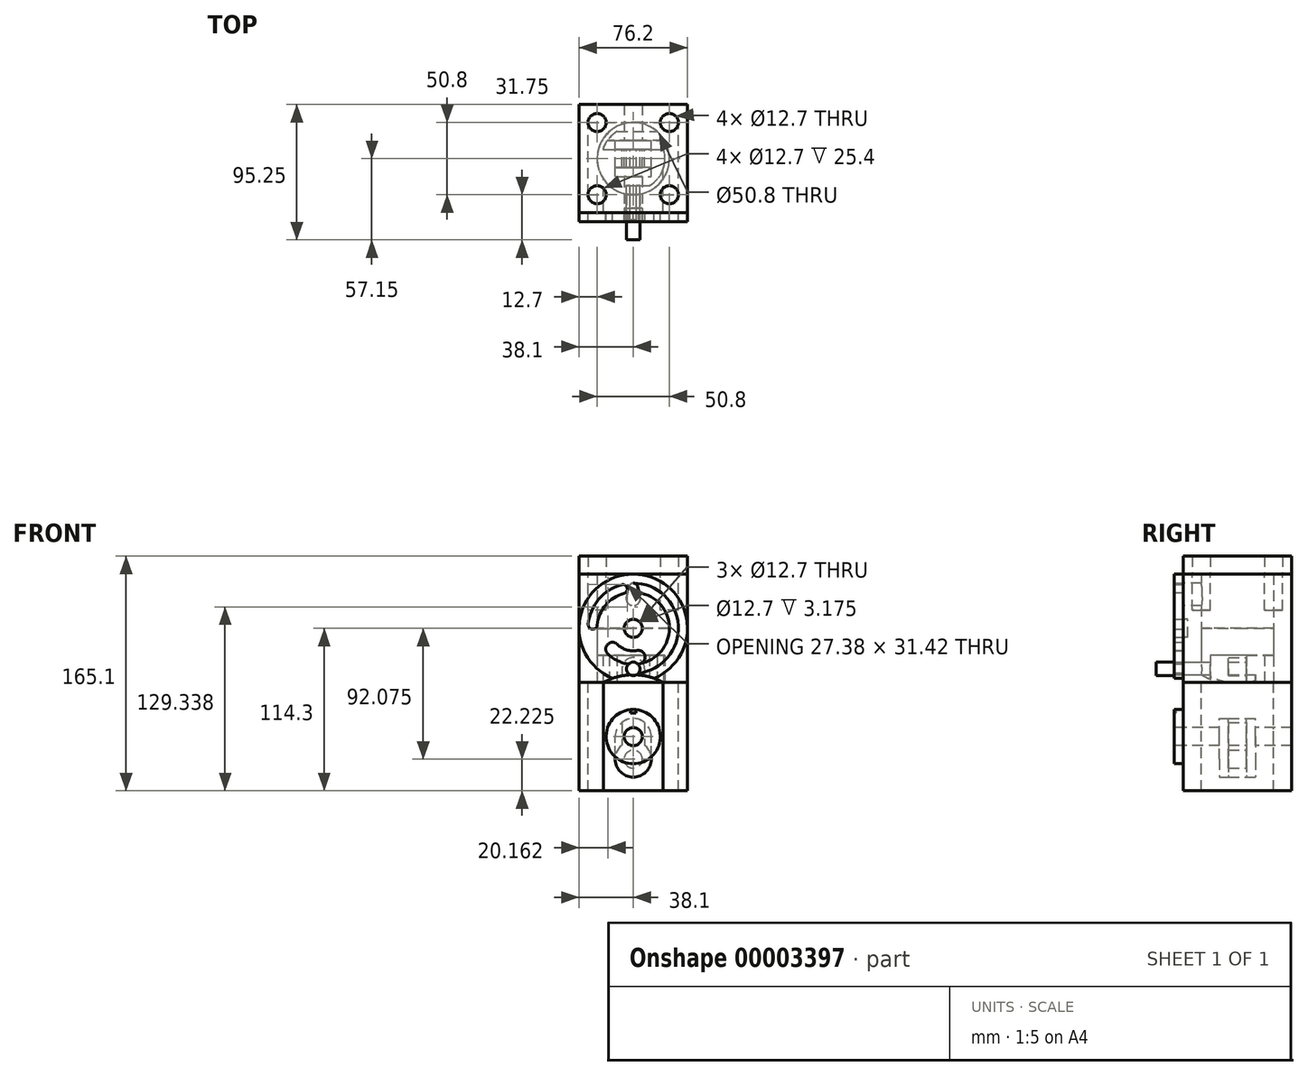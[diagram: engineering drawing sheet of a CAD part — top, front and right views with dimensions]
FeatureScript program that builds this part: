
annotation { "Feature Type Name" : "Feature", "Feature Type Description" : "" }
export const myFeature = defineFeature(function(context is Context, id is Id, definition is map)
    precondition{}
    {
        {
            var Q0;
            Q0=qCreatedBy(makeId("Top.planeOp"),FACE);
            var sketch = newSketch(context, id + "F0", { "sketchPlane" : qUnion([Q0])});
            skLineSegment(sketch, "E0.rect.bottom", {"start": v(38.1, 38.1) * mm, "end": v(-38.1, 38.1) * mm});
            skLineSegment(sketch, "E0.rect.top", {"start": v(38.1, -38.1) * mm, "end": v(-38.1, -38.1) * mm});
            skLineSegment(sketch, "E0.rect.left", {"start": v(38.1, 38.1) * mm, "end": v(38.1, -38.1) * mm});
            skLineSegment(sketch, "E0.rect.right", {"start": v(-38.1, 38.1) * mm, "end": v(-38.1, -38.1) * mm});
            skPoint(sketch, "E0.rect.middle", {"position": v(0, 0) * mm});
            skCircle(sketch, "E1", {"center": v(0, 0) * mm, "radius": 25.4 * mm});
            skSolve(sketch);
        }
        {
            var Q0;
            Q0=makeQuery(id+"F0.imprint","IMPRINT",FACE,{"disambiguationData":[TD([[makeQuery(id+"F0.imprint","IMPRINT",EDGE,{"derivedFrom":sQuery(id+"F0.wireOp",EDGE,"E0.rect.bottom")}),1.0]])]});
            extrude(context, id + "F1", {"entities" : qUnion([Q0]), "depth" : 76.2 * mm});
        }
        {
            var Q0;
            Q0=makeQuery(id+"F0.imprint","IMPRINT",FACE,{"disambiguationData":[TD([[makeQuery(id+"F0.imprint","IMPRINT",EDGE,{"derivedFrom":sQuery(id+"F0.wireOp",EDGE,"E1")}),1.0]])]});
            extrude(context, id + "F2", {"entities" : qUnion([Q0]), "depth" : 38.1 * mm});
        }
        {
            var Q0;
            Q0=makeQuery(id+"F1.opExtrude","CAP_FACE",FACE,{"disambiguationData":[OSD([sQuery(id+"F0.wireOp",EDGE,"E0.rect.bottom"),sQuery(id+"F0.wireOp",EDGE,"E0.rect.top"),sQuery(id+"F0.wireOp",EDGE,"E0.rect.left"),sQuery(id+"F0.wireOp",EDGE,"E0.rect.right"),sQuery(id+"F0.wireOp",EDGE,"E1")])],"isStart":false});
            var sketch = newSketch(context, id + "F3", { "sketchPlane" : qUnion([Q0])});
            skCircle(sketch, "E2", {"center": v(25.4, -25.4) * mm, "radius": 6.35 * mm});
            skCircle(sketch, "E3", {"center": v(25.4, 25.4) * mm, "radius": 6.35 * mm});
            skCircle(sketch, "E4", {"center": v(-25.4, 25.4) * mm, "radius": 6.35 * mm});
            skCircle(sketch, "E5", {"center": v(-25.4, -25.4) * mm, "radius": 6.35 * mm});
            skPoint(sketch, "E6.0", {"position": v(-38.1, 38.1) * mm});
            skPoint(sketch, "E7.0", {"position": v(38.1, -38.1) * mm});
            skSolve(sketch);
        }
        {
            var Q0;
            Q0=makeQuery(id+"F3.imprint","IMPRINT",FACE,{"disambiguationData":[TD([[makeQuery(id+"F3.imprint","IMPRINT",EDGE,{"derivedFrom":sQuery(id+"F3.wireOp",EDGE,"E4")}),1.0]])]});
            var Q1;
            Q1=makeQuery(id+"F3.imprint","IMPRINT",FACE,{"disambiguationData":[TD([[makeQuery(id+"F3.imprint","IMPRINT",EDGE,{"derivedFrom":sQuery(id+"F3.wireOp",EDGE,"E3")}),1.0]])]});
            var Q2;
            Q2=makeQuery(id+"F3.imprint","IMPRINT",FACE,{"disambiguationData":[TD([[makeQuery(id+"F3.imprint","IMPRINT",EDGE,{"derivedFrom":sQuery(id+"F3.wireOp",EDGE,"E2")}),1.0]])]});
            var Q3;
            Q3=makeQuery(id+"F3.imprint","IMPRINT",FACE,{"disambiguationData":[TD([[makeQuery(id+"F3.imprint","IMPRINT",EDGE,{"derivedFrom":sQuery(id+"F3.wireOp",EDGE,"E5")}),1.0]])]});
            extrude(context, id + "F4", {"entities" : qUnion([Q0, Q1, Q2, Q3]), "operationType" : NewBodyOperationType.REMOVE, "oppositeDirection" : true, "depth" : 25.4 * mm});
        }
        {
            var Q0;
            Q0=makeQuery(id+"F3.imprint","IMPRINT",FACE,{"disambiguationData":[TD([[makeQuery(id+"F3.imprint","IMPRINT",EDGE,{"derivedFrom":sQuery(id+"F3.wireOp",EDGE,"E2")}),-1.0]])]});
            var Q1;
            Q1=makeQuery(id+"F3.imprint","IMPRINT",FACE,{"disambiguationData":[TD([[makeQuery(id+"F3.imprint","IMPRINT",EDGE,{"derivedFrom":makeQuery(id+"F1.opExtrude","CAP_EDGE",EDGE,{"disambiguationData":[OSD([sQuery(id+"F0.wireOp",EDGE,"E1")])],"isStart":false})}),1.0]])]});
            extrude(context, id + "F5", {"entities" : qUnion([Q0, Q1]), "depth" : 12.7 * mm});
        }
        {
            var Q0;
            Q0=qCreatedBy(makeId("Right.planeOp"),FACE);
            var sketch = newSketch(context, id + "F6", { "sketchPlane" : qUnion([Q0])});
            skLineSegment(sketch, "E8", {"start": v(-107.9, -38.1) * mm, "end": v(101.54, -38.1) * mm});
            skLineSegment(sketch, "E9", {"start": v(-103.78, -53.98) * mm, "end": v(66.08, -53.97) * mm});
            skLineSegment(sketch, "E10.rect.bottom", {"start": v(38.1, -44.45) * mm, "end": v(-44.45, -44.45) * mm});
            skLineSegment(sketch, "E10.rect.top", {"start": v(38.1, -31.75) * mm, "end": v(-44.45, -31.75) * mm});
            skLineSegment(sketch, "E10.rect.left", {"start": v(38.1, -44.45) * mm, "end": v(38.1, -31.75) * mm});
            skLineSegment(sketch, "E10.rect.right", {"start": v(-44.45, -44.45) * mm, "end": v(-44.45, -31.75) * mm});
            skPoint(sketch, "E10.rect.middle", {"position": v(-3.17, -38.1) * mm});
            skLineSegment(sketch, "E11.rect.bottom", {"start": v(-6.35, -66.68) * mm, "end": v(-12.7, -66.68) * mm});
            skLineSegment(sketch, "E11.rect.top", {"start": v(-6.35, -9.52) * mm, "end": v(-12.7, -9.52) * mm});
            skLineSegment(sketch, "E11.rect.left", {"start": v(-6.35, -66.67) * mm, "end": v(-6.35, -9.52) * mm});
            skLineSegment(sketch, "E11.rect.right", {"start": v(-12.7, -66.68) * mm, "end": v(-12.7, -9.52) * mm});
            skPoint(sketch, "E11.rect.middle", {"position": v(-9.53, -38.1) * mm});
            skLineSegment(sketch, "E12.rect.bottom", {"start": v(6.35, -60.33) * mm, "end": v(-6.35, -60.33) * mm});
            skLineSegment(sketch, "E12.rect.top", {"start": v(6.35, -47.63) * mm, "end": v(-6.35, -47.63) * mm});
            skLineSegment(sketch, "E12.rect.left", {"start": v(6.35, -60.33) * mm, "end": v(6.35, -47.63) * mm});
            skLineSegment(sketch, "E12.rect.right", {"start": v(-6.35, -60.33) * mm, "end": v(-6.35, -47.63) * mm});
            skPoint(sketch, "E12.rect.middle", {"position": v(0, -53.98) * mm});
            skLineSegment(sketch, "E13.rect.bottom", {"start": v(12.7, -66.67) * mm, "end": v(6.35, -66.67) * mm});
            skLineSegment(sketch, "E13.rect.top", {"start": v(12.7, -9.52) * mm, "end": v(6.35, -9.52) * mm});
            skLineSegment(sketch, "E13.rect.left", {"start": v(12.7, -66.67) * mm, "end": v(12.7, -9.52) * mm});
            skLineSegment(sketch, "E13.rect.right", {"start": v(6.35, -66.67) * mm, "end": v(6.35, -9.52) * mm});
            skPoint(sketch, "E13.rect.middle", {"position": v(9.52, -38.1) * mm});
            skLineSegment(sketch, "E14.0", {"start": v(38.1, 0) * mm, "end": v(-38.1, 0) * mm, "construction": true});
            skSolve(sketch);
        }
        {
            var Q0;
            {var subQ1=sQuery(id+"F6.wireOp",EDGE,"E8");var subQ5=sQuery(id+"F6.wireOp",EDGE,"E10.rect.right");var subQ6=makeQuery(id+"F6.imprint","INTERSECT",VERTEX,{"derivedFrom":[subQ1,subQ5]});Q0=makeQuery(id+"F6.imprint","IMPRINT",FACE,{"disambiguationData":[TD([[makeQuery(id+"F6.imprint","IMPRINT",EDGE,{"disambiguationData":[TD([[subQ6,-1.0]])],"derivedFrom":subQ1}),1.0]])]});}
            var Q1;
            {var subQ0=sQuery(id+"F6.wireOp",EDGE,"E11.rect.right");var subQ1=sQuery(id+"F6.wireOp",EDGE,"E8");var subQ2=makeQuery(id+"F6.imprint","INTERSECT",VERTEX,{"derivedFrom":[subQ1,subQ0]});Q1=makeQuery(id+"F6.imprint","IMPRINT",FACE,{"disambiguationData":[TD([[makeQuery(id+"F6.imprint","IMPRINT",EDGE,{"disambiguationData":[TD([[subQ2,-1.0]])],"derivedFrom":subQ1}),1.0]])]});}
            var Q2;
            {var subQ3=sQuery(id+"F6.wireOp",EDGE,"E11.rect.bottom");Q2=makeQuery(id+"F6.imprint","IMPRINT",FACE,{"disambiguationData":[TD([[makeQuery(id+"F6.imprint","IMPRINT",EDGE,{"derivedFrom":subQ3}),-1.0]])]});}
            var Q3;
            {var subQ3=sQuery(id+"F6.wireOp",EDGE,"E11.rect.top");Q3=makeQuery(id+"F6.imprint","IMPRINT",FACE,{"disambiguationData":[TD([[makeQuery(id+"F6.imprint","IMPRINT",EDGE,{"derivedFrom":subQ3}),1.0]])]});}
            var Q4;
            {var subQ0=sQuery(id+"F6.wireOp",EDGE,"E13.rect.right");var subQ1=sQuery(id+"F6.wireOp",EDGE,"E8");var subQ2=makeQuery(id+"F6.imprint","INTERSECT",VERTEX,{"derivedFrom":[subQ1,subQ0]});Q4=makeQuery(id+"F6.imprint","IMPRINT",FACE,{"disambiguationData":[TD([[makeQuery(id+"F6.imprint","IMPRINT",EDGE,{"disambiguationData":[TD([[subQ2,-1.0]])],"derivedFrom":subQ1}),1.0]])]});}
            var Q5;
            {var subQ4=sQuery(id+"F6.wireOp",EDGE,"E13.rect.bottom");Q5=makeQuery(id+"F6.imprint","IMPRINT",FACE,{"disambiguationData":[TD([[makeQuery(id+"F6.imprint","IMPRINT",EDGE,{"derivedFrom":subQ4}),-1.0]])]});}
            var Q6;
            {var subQ3=sQuery(id+"F6.wireOp",EDGE,"E13.rect.top");Q6=makeQuery(id+"F6.imprint","IMPRINT",FACE,{"disambiguationData":[TD([[makeQuery(id+"F6.imprint","IMPRINT",EDGE,{"derivedFrom":subQ3}),1.0]])]});}
            var Q7;
            {var subQ1=sQuery(id+"F6.wireOp",EDGE,"E8");var subQ5=sQuery(id+"F6.wireOp",EDGE,"E10.rect.left");var subQ6=makeQuery(id+"F6.imprint","INTERSECT",VERTEX,{"derivedFrom":[subQ1,subQ5]});Q7=makeQuery(id+"F6.imprint","IMPRINT",FACE,{"disambiguationData":[TD([[makeQuery(id+"F6.imprint","IMPRINT",EDGE,{"disambiguationData":[TD([[subQ6,1.0]])],"derivedFrom":subQ1}),1.0]])]});}
            var Q8;
            Q8=sQuery(id+"F6.wireOp",EDGE,"E8");
            revolve(context, id + "F7", {"entities" : qUnion([Q0, Q1, Q2, Q3, Q4, Q5, Q6, Q7]), "axis" : qUnion([Q8]), "revolveType" : RevolveType.FULL});
        }
        {
            var Q0;
            {var subQ3=sQuery(id+"F6.wireOp",EDGE,"E12.rect.top");Q0=makeQuery(id+"F6.imprint","IMPRINT",FACE,{"disambiguationData":[TD([[makeQuery(id+"F6.imprint","IMPRINT",EDGE,{"derivedFrom":subQ3}),1.0]])]});}
            var Q1;
            Q1=sQuery(id+"F6.wireOp",EDGE,"E9");
            revolve(context, id + "F8", {"operationType" : NewBodyOperationType.ADD, "entities" : qUnion([Q0]), "axis" : qUnion([Q1]), "revolveType" : RevolveType.FULL});
        }
        {
            var Q0;
            Q0=makeQuery(id+"F2.opExtrude","CAP_FACE",FACE,{"disambiguationData":[OSD([sQuery(id+"F0.wireOp",EDGE,"E1")])],"isStart":true});
            var sketch = newSketch(context, id + "F9", { "sketchPlane" : qUnion([Q0])});
            skLineSegment(sketch, "E15.rect.bottom", {"start": v(-21.3, -6.35) * mm, "end": v(21.3, -6.35) * mm});
            skLineSegment(sketch, "E15.rect.top", {"start": v(-21.3, 6.35) * mm, "end": v(21.3, 6.35) * mm});
            skLineSegment(sketch, "E15.rect.left", {"start": v(-21.3, -6.35) * mm, "end": v(-21.3, 6.35) * mm, "construction": true});
            skLineSegment(sketch, "E15.rect.right", {"start": v(21.3, -6.35) * mm, "end": v(21.3, 6.35) * mm, "construction": true});
            skPoint(sketch, "E15.rect.middle", {"position": v(0, 0) * mm});
            skCircle(sketch, "E16", {"center": v(0, 0) * mm, "radius": 22.23 * mm});
            skLineSegment(sketch, "E17", {"start": v(-16.8, 19.05) * mm, "end": v(16.8, 19.05) * mm});
            skCircle(sketch, "E18.0", {"center": v(0, 0) * mm, "radius": 25.4 * mm});
            skLineSegment(sketch, "E19", {"start": v(0, 0) * mm, "end": v(-10.7, 0) * mm, "construction": true});
            skLineSegment(sketch, "E20.0.MirrorCS", {"start": v(-16.8, -19.05) * mm, "end": v(16.8, -19.05) * mm});
            skSolve(sketch);
        }
        {
            var Q0;
            {var subQ2=sQuery(id+"F9.wireOp",EDGE,"E15.rect.bottom");Q0=makeQuery(id+"F9.imprint","IMPRINT",FACE,{"disambiguationData":[TD([[makeQuery(id+"F9.imprint","IMPRINT",EDGE,{"derivedFrom":subQ2}),1.0]])]});}
            var Q1;
            {var subQ0=sQuery(id+"F9.wireOp",EDGE,"E17");var subQ1=sQuery(id+"F9.wireOp",EDGE,"E16");var subQ3=makeQuery(id+"F9.imprint","INTERSECT",VERTEX,{"disambiguationData":[OD(0.0)],"derivedFrom":[subQ1,subQ0]});Q1=makeQuery(id+"F9.imprint","IMPRINT",FACE,{"disambiguationData":[TD([[makeQuery(id+"F9.imprint","IMPRINT",EDGE,{"disambiguationData":[TD([[subQ3,-1.0]])],"derivedFrom":subQ1}),1.0]])]});}
            var Q2;
            {var subQ1=sQuery(id+"F9.wireOp",EDGE,"E17");var subQ4=sQuery(id+"F9.wireOp",EDGE,"E16");var subQ5=makeQuery(id+"F9.imprint","INTERSECT",VERTEX,{"disambiguationData":[OD(0.0)],"derivedFrom":[subQ4,subQ1]});Q2=makeQuery(id+"F9.imprint","IMPRINT",FACE,{"disambiguationData":[TD([[makeQuery(id+"F9.imprint","IMPRINT",EDGE,{"disambiguationData":[TD([[subQ5,-1.0]])],"derivedFrom":subQ4}),-1.0]])]});}
            var Q3;
            {var subQ0=sQuery(id+"F9.wireOp",EDGE,"E17");var subQ1=sQuery(id+"F9.wireOp",EDGE,"E16");var subQ3=makeQuery(id+"F9.imprint","INTERSECT",VERTEX,{"disambiguationData":[OD(0.0)],"derivedFrom":[subQ1,subQ0]});var subQ4=sQuery(id+"F9.wireOp",EDGE,"E20.0.MirrorCS");var subQ6=makeQuery(id+"F9.imprint","INTERSECT",VERTEX,{"disambiguationData":[OD(0.0)],"derivedFrom":[subQ1,subQ4]});Q3=qUnion([makeQuery(id+"F9.imprint","IMPRINT",FACE,{"disambiguationData":[TD([[makeQuery(id+"F9.imprint","IMPRINT",EDGE,{"disambiguationData":[TD([[subQ3,-1.0]])],"derivedFrom":subQ1}),1.0]])]}),makeQuery(id+"F9.imprint","IMPRINT",FACE,{"disambiguationData":[TD([[makeQuery(id+"F9.imprint","IMPRINT",EDGE,{"disambiguationData":[TD([[subQ6,-1.0]])],"derivedFrom":subQ1}),1.0]])]})]);}
            var Q4;
            {var subQ0=sQuery(id+"F9.wireOp",EDGE,"E20.0.MirrorCS");var subQ1=sQuery(id+"F9.wireOp",EDGE,"E16");var subQ5=makeQuery(id+"F9.imprint","INTERSECT",VERTEX,{"disambiguationData":[OD(0.0)],"derivedFrom":[subQ1,subQ0]});Q4=makeQuery(id+"F9.imprint","IMPRINT",FACE,{"disambiguationData":[TD([[makeQuery(id+"F9.imprint","IMPRINT",EDGE,{"disambiguationData":[TD([[subQ5,-1.0]])],"derivedFrom":subQ1}),-1.0]])]});}
            extrude(context, id + "F10", {"entities" : qUnion([Q0, Q1, Q2, Q3, Q4]), "operationType" : NewBodyOperationType.REMOVE, "oppositeDirection" : true, "depth" : 19.05 * mm});
        }
        {
            var Q0;
            Q0=makeQuery(id+"F10.boolean.opBoolean","COPY",FACE,{"derivedFrom":makeQuery(id+"F10.opExtrude","SWEPT_FACE",FACE,{"disambiguationData":[OSD([sQuery(id+"F9.wireOp",EDGE,"E17")])]})});
            var sketch = newSketch(context, id + "F11", { "sketchPlane" : qUnion([Q0])});
            skCircle(sketch, "E21", {"center": v(0, 9.53) * mm, "radius": 4.76 * mm});
            skLineSegment(sketch, "E22", {"start": v(-16.8, 0) * mm, "end": v(16.8, 19.05) * mm, "construction": true});
            skSolve(sketch);
        }
        {
            var Q0;
            Q0=makeQuery(id+"F11.imprint","IMPRINT",FACE,{"disambiguationData":[TD([[makeQuery(id+"F11.imprint","IMPRINT",EDGE,{"derivedFrom":sQuery(id+"F11.wireOp",EDGE,"E21")}),1.0]])]});
            extrude(context, id + "F12", {"entities" : qUnion([Q0]), "operationType" : NewBodyOperationType.REMOVE, "endBound" : BoundingType.THROUGH_ALL, "oppositeDirection" : true, "depth" : 25.4 * mm});
        }
        {
            var Q0;
            Q0=qCreatedBy(makeId("Front.planeOp"),FACE);
            var sketch = newSketch(context, id + "F13", { "sketchPlane" : qUnion([Q0])});
            skCircle(sketch, "E23.0", {"center": v(0, -53.98) * mm, "radius": 6.35 * mm});
            skCircle(sketch, "E23.1", {"center": v(0, 9.53) * mm, "radius": 4.76 * mm});
            skLineSegment(sketch, "E24.0", {"start": v(-21.3, 19.05) * mm, "end": v(21.3, 19.05) * mm});
            skCircle(sketch, "E25", {"center": v(0, 9.53) * mm, "radius": 7.94 * mm});
            skCircle(sketch, "E26", {"center": v(0, -53.98) * mm, "radius": 12.7 * mm});
            skLineSegment(sketch, "E27", {"start": v(7.94, 9.53) * mm, "end": v(7.94, -44.06) * mm});
            skLineSegment(sketch, "E28", {"start": v(-7.94, 9.52) * mm, "end": v(-7.94, -44.06) * mm});
            skSolve(sketch);
        }
        {
            var Q0;
            Q0=makeQuery(id+"F13.imprint","IMPRINT",FACE,{"disambiguationData":[TD([[makeQuery(id+"F13.imprint","IMPRINT",EDGE,{"derivedFrom":sQuery(id+"F13.wireOp",EDGE,"E23.1")}),-1.0]])]});
            var Q1;
            {var subQ1=sQuery(id+"F13.wireOp",EDGE,"E27");Q1=makeQuery(id+"F13.imprint","IMPRINT",FACE,{"disambiguationData":[TD([[makeQuery(id+"F13.imprint","IMPRINT",EDGE,{"derivedFrom":subQ1}),-1.0]])]});}
            var Q2;
            Q2=makeQuery(id+"F13.imprint","IMPRINT",FACE,{"disambiguationData":[TD([[makeQuery(id+"F13.imprint","IMPRINT",EDGE,{"derivedFrom":sQuery(id+"F13.wireOp",EDGE,"E23.0")}),-1.0]])]});
            extrude(context, id + "F14", {"entities" : qUnion([Q0, Q1, Q2]), "endBound" : BoundingType.SYMMETRIC, "depth" : 12.7 * mm});
        }
        {
            var Q0;
            Q0=makeQuery(id+"F11.imprint","IMPRINT",FACE,{"disambiguationData":[TD([[makeQuery(id+"F11.imprint","IMPRINT",EDGE,{"derivedFrom":sQuery(id+"F11.wireOp",EDGE,"E21")}),1.0]])]});
            extrude(context, id + "F15", {"entities" : qUnion([Q0]), "oppositeDirection" : true, "depth" : 38.1 * mm});
        }
        {
            var Q0;
            {var subQ0=sQuery(id+"F6.wireOp",EDGE,"E13.rect.left");Q0=makeQuery(id+"F7.opRevolve","SWEPT_FACE",FACE,{"disambiguationData":[OSD([subQ0]),TDD([makeQuery(id+"F6.imprint","IMPRINT",EDGE,{"disambiguationData":[TD([[makeQuery(id+"F6.imprint","INTERSECT",VERTEX,{"derivedFrom":[sQuery(id+"F6.wireOp",EDGE,"E13.rect.top"),subQ0]}),1.0]])],"derivedFrom":subQ0})])]});}
            var sketch = newSketch(context, id + "F16", { "sketchPlane" : qUnion([Q0])});
            skArc(sketch, "E29.0.0", {"start": v(-7.94, 9.53) * mm, "mid": v(0, 17.46) * mm, "end": v(7.94, 9.52) * mm});
            skArc(sketch, "E29.0.2", {"start": v(7.94, -44.06) * mm, "mid": v(0, -66.67) * mm, "end": v(-7.94, -44.06) * mm});
            skCircle(sketch, "E30.0", {"center": v(0, -38.1) * mm, "radius": 6.35 * mm});
            skArc(sketch, "E31", {"start": v(12.7, -38.1) * mm, "mid": v(0, -25.4) * mm, "end": v(-12.7, -38.1) * mm});
            skLineSegment(sketch, "E32", {"start": v(12.7, -38.1) * mm, "end": v(12.7, -53.98) * mm});
            skLineSegment(sketch, "E33", {"start": v(-12.7, -38.1) * mm, "end": v(-12.7, -53.98) * mm});
            skCircle(sketch, "E34", {"center": v(0, -38.1) * mm, "radius": 43.5 * mm});
            skSolve(sketch);
        }
        {
            var Q0;
            Q0=makeQuery(id+"F16.imprint","IMPRINT",FACE,{"disambiguationData":[TD([[makeQuery(id+"F16.imprint","IMPRINT",EDGE,{"derivedFrom":sQuery(id+"F16.wireOp",EDGE,"E34")}),1.0]])]});
            var Q1;
            Q1=makeQuery(id+"F16.imprint","IMPRINT",FACE,{"disambiguationData":[TD([[makeQuery(id+"F16.imprint","IMPRINT",EDGE,{"derivedFrom":sQuery(id+"F16.wireOp",EDGE,"E31")}),-1.0]])]});
            extrude(context, id + "F17", {"entities" : qUnion([Q0, Q1]), "operationType" : NewBodyOperationType.REMOVE, "oppositeDirection" : true, "depth" : 57.32 * mm});
        }
        {
            var Q0;
            Q0=makeQuery(id+"F1.opExtrude","CAP_FACE",FACE,{"disambiguationData":[OSD([sQuery(id+"F0.wireOp",EDGE,"E0.rect.bottom"),sQuery(id+"F0.wireOp",EDGE,"E0.rect.top"),sQuery(id+"F0.wireOp",EDGE,"E0.rect.left"),sQuery(id+"F0.wireOp",EDGE,"E0.rect.right"),sQuery(id+"F0.wireOp",EDGE,"E1")])],"isStart":true});
            var sketch = newSketch(context, id + "F18", { "sketchPlane" : qUnion([Q0])});
            skLineSegment(sketch, "E35.0", {"start": v(-38.1, -38.1) * mm, "end": v(-38.1, 38.1) * mm});
            skLineSegment(sketch, "E35.1", {"start": v(38.1, 38.1) * mm, "end": v(-38.1, 38.1) * mm});
            skLineSegment(sketch, "E35.2", {"start": v(38.1, -38.1) * mm, "end": v(-38.1, -38.1) * mm});
            skLineSegment(sketch, "E35.3", {"start": v(38.1, -38.1) * mm, "end": v(38.1, 38.1) * mm});
            skLineSegment(sketch, "E36.rect.bottom", {"start": v(-31.75, 25.4) * mm, "end": v(31.75, 25.4) * mm});
            skLineSegment(sketch, "E36.rect.top", {"start": v(-31.75, -25.4) * mm, "end": v(31.75, -25.4) * mm});
            skLineSegment(sketch, "E36.rect.left", {"start": v(-31.75, 25.4) * mm, "end": v(-31.75, -25.4) * mm});
            skLineSegment(sketch, "E36.rect.right", {"start": v(31.75, 25.4) * mm, "end": v(31.75, -25.4) * mm});
            skPoint(sketch, "E36.rect.middle", {"position": v(0, 0) * mm});
            skSolve(sketch);
        }
        {
            var Q0;
            Q0=makeQuery(id+"F18.imprint","IMPRINT",FACE,{"disambiguationData":[TD([[makeQuery(id+"F18.imprint","IMPRINT",EDGE,{"derivedFrom":sQuery(id+"F18.wireOp",EDGE,"E35.0")}),-1.0]])]});
            extrude(context, id + "F19", {"entities" : qUnion([Q0]), "depth" : 76.2 * mm});
        }
        {
            var Q0;
            Q0=makeQuery(id+"F7.opRevolve","SWEPT_BODY",BODY,{"disambiguationData":[OSD([sQuery(id+"F6.wireOp",EDGE,"E8"),sQuery(id+"F6.wireOp",EDGE,"E10.rect.top"),sQuery(id+"F6.wireOp",EDGE,"E10.rect.right"),sQuery(id+"F6.wireOp",EDGE,"E11.rect.top"),sQuery(id+"F6.wireOp",EDGE,"E11.rect.left"),sQuery(id+"F6.wireOp",EDGE,"E11.rect.right")])]});
            var Q1;
            Q1=makeQuery(id+"F19.opExtrude","SWEPT_BODY",BODY,{"disambiguationData":[OSD([sQuery(id+"F18.wireOp",EDGE,"E35.0"),sQuery(id+"F18.wireOp",EDGE,"E35.1"),sQuery(id+"F18.wireOp",EDGE,"E35.2"),sQuery(id+"F18.wireOp",EDGE,"E35.3"),sQuery(id+"F18.wireOp",EDGE,"E36.rect.bottom"),sQuery(id+"F18.wireOp",EDGE,"E36.rect.top"),sQuery(id+"F18.wireOp",EDGE,"E36.rect.left"),sQuery(id+"F18.wireOp",EDGE,"E36.rect.right")])]});
            booleanBodies(context, id + "F20", {"operationType" : BooleanOperationType.SUBTRACTION, "tools" : qUnion([Q0]), "targets" : qUnion([Q1]), "keepTools" : true});
        }
        {
            var Q0;
            Q0=makeQuery(id+"F1.opExtrude","SWEPT_FACE",FACE,{"disambiguationData":[OSD([sQuery(id+"F0.wireOp",EDGE,"E0.rect.top")])]});
            var sketch = newSketch(context, id + "F21", { "sketchPlane" : qUnion([Q0])});
            skLineSegment(sketch, "E37", {"start": v(-38.1, 0) * mm, "end": v(38.1, 76.2) * mm, "construction": true});
            skCircle(sketch, "E38", {"center": v(0, 38.1) * mm, "radius": 31.75 * mm});
            skCircle(sketch, "E39", {"center": v(0, 38.1) * mm, "radius": 25.4 * mm});
            skCircle(sketch, "E40", {"center": v(0, 38.1) * mm, "radius": 15.88 * mm});
            skArc(sketch, "E41", {"start": v(-6.57, 62.63) * mm, "mid": v(-4.33, 66.52) * mm, "end": v(-8.22, 68.77) * mm});
            skLineSegment(sketch, "E42", {"start": v(0, 38.1) * mm, "end": v(-38.1, 38.1) * mm, "construction": true});
            skLineSegment(sketch, "E43", {"start": v(0, 38.1) * mm, "end": v(-7.4, 65.7) * mm, "construction": true});
            skArc(sketch, "E44", {"start": v(-31.63, 40.87) * mm, "mid": v(-28.74, 37.43) * mm, "end": v(-25.3, 40.31) * mm});
            skLineSegment(sketch, "E45", {"start": v(0, 38.1) * mm, "end": v(-28.47, 40.6) * mm, "construction": true});
            skArc(sketch, "E46", {"start": v(-11.23, 26.87) * mm, "mid": v(-17.96, 26.87) * mm, "end": v(-17.96, 20.14) * mm});
            skArc(sketch, "E47", {"start": v(4.41, 13.09) * mm, "mid": v(8.27, 18.6) * mm, "end": v(2.76, 22.47) * mm});
            skLineSegment(sketch, "E48", {"start": v(0, 38.1) * mm, "end": v(-14.6, 23.5) * mm, "construction": true});
            skLineSegment(sketch, "E49", {"start": v(0, 38.1) * mm, "end": v(3.58, 17.78) * mm, "construction": true});
            skCircle(sketch, "E50", {"center": v(0, 38.1) * mm, "radius": 38.1 * mm});
            skCircle(sketch, "E51", {"center": v(0, 38.1) * mm, "radius": 6.35 * mm});
            skArc(sketch, "E52", {"start": v(3.11, 67.3) * mm, "mid": v(0, 69.85) * mm, "end": v(-3.11, 67.3) * mm});
            skArc(sketch, "E53", {"start": v(-4.67, 59.69) * mm, "mid": v(0, 53.97) * mm, "end": v(4.67, 59.69) * mm});
            skLineSegment(sketch, "E54", {"start": v(3.11, 67.3) * mm, "end": v(4.67, 59.69) * mm});
            skLineSegment(sketch, "E55", {"start": v(-4.67, 59.69) * mm, "end": v(-3.11, 67.3) * mm});
            skSolve(sketch);
        }
        {
            var Q0;
            {var subQ7=sQuery(id+"F21.wireOp",EDGE,"E41");Q0=makeQuery(id+"F21.imprint","IMPRINT",FACE,{"disambiguationData":[TD([[makeQuery(id+"F21.imprint","IMPRINT",EDGE,{"derivedFrom":subQ7}),-1.0]])]});}
            var Q1;
            {var subQ6=sQuery(id+"F21.wireOp",EDGE,"E38");var subQ9=makeQuery(id+"F21.imprint","INTERSECT",VERTEX,{"derivedFrom":[subQ6,sQuery(id+"F21.wireOp",EDGE,"E41")]});Q1=makeQuery(id+"F21.imprint","IMPRINT",FACE,{"disambiguationData":[TD([[makeQuery(id+"F21.imprint","IMPRINT",EDGE,{"disambiguationData":[TD([[subQ9,1.0]])],"derivedFrom":subQ6}),-1.0]])]});}
            var Q2;
            {var subQ7=sQuery(id+"F21.wireOp",EDGE,"E46");Q2=makeQuery(id+"F21.imprint","IMPRINT",FACE,{"disambiguationData":[TD([[makeQuery(id+"F21.imprint","IMPRINT",EDGE,{"derivedFrom":subQ7}),-1.0]])]});}
            var Q3;
            Q3=makeQuery(id+"F21.imprint","IMPRINT",FACE,{"disambiguationData":[TD([[makeQuery(id+"F21.imprint","IMPRINT",EDGE,{"derivedFrom":sQuery(id+"F21.wireOp",EDGE,"E51")}),-1.0]])]});
            var Q4;
            {var subQ0=sQuery(id+"F21.wireOp",EDGE,"E55");var subQ1=sQuery(id+"F21.wireOp",EDGE,"E39");var subQ2=makeQuery(id+"F21.imprint","INTERSECT",VERTEX,{"derivedFrom":[subQ1,subQ0]});Q4=makeQuery(id+"F21.imprint","IMPRINT",FACE,{"disambiguationData":[TD([[makeQuery(id+"F21.imprint","IMPRINT",EDGE,{"disambiguationData":[TD([[subQ2,1.0]])],"derivedFrom":subQ1}),1.0]])]});}
            var Q5;
            {var subQ0=sQuery(id+"F21.wireOp",EDGE,"E55");var subQ1=sQuery(id+"F21.wireOp",EDGE,"E39");var subQ2=makeQuery(id+"F21.imprint","INTERSECT",VERTEX,{"derivedFrom":[subQ1,subQ0]});Q5=makeQuery(id+"F21.imprint","IMPRINT",FACE,{"disambiguationData":[TD([[makeQuery(id+"F21.imprint","IMPRINT",EDGE,{"disambiguationData":[TD([[subQ2,1.0]])],"derivedFrom":subQ1}),-1.0]])]});}
            var Q6;
            {var subQ9=sQuery(id+"F21.wireOp",EDGE,"E44");Q6=makeQuery(id+"F21.imprint","IMPRINT",FACE,{"disambiguationData":[TD([[makeQuery(id+"F21.imprint","IMPRINT",EDGE,{"derivedFrom":subQ9}),-1.0]])]});}
            var Q7;
            {var subQ7=sQuery(id+"F21.wireOp",EDGE,"E47");Q7=makeQuery(id+"F21.imprint","IMPRINT",FACE,{"disambiguationData":[TD([[makeQuery(id+"F21.imprint","IMPRINT",EDGE,{"derivedFrom":subQ7}),-1.0]])]});}
            extrude(context, id + "F22", {"entities" : qUnion([Q0, Q1, Q2, Q3, Q4, Q5, Q6, Q7]), "depth" : 6.35 * mm});
        }
        {
            var Q0;
            Q0=makeQuery(id+"F21.imprint","IMPRINT",FACE,{"disambiguationData":[TD([[makeQuery(id+"F21.imprint","IMPRINT",EDGE,{"derivedFrom":sQuery(id+"F21.wireOp",EDGE,"E51")}),1.0]])]});
            var Q1;
            Q1=sQuery(id+"F21.wireOp",EDGE,"E51");
            extrude(context, id + "F23", {"entities" : qUnion([Q0]), "operationType" : NewBodyOperationType.REMOVE, "surfaceEntities" : qUnion([Q1]), "oppositeDirection" : true, "depth" : 3.17 * mm});
        }
        {
            var Q0;
            Q0=makeQuery(id+"F23.boolean.opBoolean","COPY",FACE,{"derivedFrom":makeQuery(id+"F23.opExtrude","CAP_FACE",FACE,{"disambiguationData":[OSD([sQuery(id+"F21.wireOp",EDGE,"E51")])],"isStart":false})});
            var Q1;
            Q1=makeQuery(id+"F22.opExtrude","CAP_FACE",FACE,{"disambiguationData":[OSD([sQuery(id+"F21.wireOp",EDGE,"E38"),sQuery(id+"F21.wireOp",EDGE,"E39"),sQuery(id+"F21.wireOp",EDGE,"E40"),sQuery(id+"F21.wireOp",EDGE,"E41"),sQuery(id+"F21.wireOp",EDGE,"E44"),sQuery(id+"F21.wireOp",EDGE,"E46"),sQuery(id+"F21.wireOp",EDGE,"E47"),sQuery(id+"F21.wireOp",EDGE,"E50"),sQuery(id+"F21.wireOp",EDGE,"E51")])],"isStart":false});
            extrude(context, id + "F24", {"entities" : qUnion([Q0]), "endBound" : BoundingType.UP_TO_SURFACE, "endBoundEntityFace" : qUnion([Q1]), "depth" : 25.4 * mm});
        }
        {
            var Q0;
            {var subQ0=sQuery(id+"F21.wireOp",EDGE,"E55");var subQ1=sQuery(id+"F21.wireOp",EDGE,"E39");var subQ2=makeQuery(id+"F21.imprint","INTERSECT",VERTEX,{"derivedFrom":[subQ1,subQ0]});Q0=makeQuery(id+"F21.imprint","IMPRINT",FACE,{"disambiguationData":[TD([[makeQuery(id+"F21.imprint","IMPRINT",EDGE,{"disambiguationData":[TD([[subQ2,1.0]])],"derivedFrom":subQ1}),1.0]])]});}
            var Q1;
            {var subQ0=sQuery(id+"F21.wireOp",EDGE,"E55");var subQ1=sQuery(id+"F21.wireOp",EDGE,"E39");var subQ2=makeQuery(id+"F21.imprint","INTERSECT",VERTEX,{"derivedFrom":[subQ1,subQ0]});Q1=makeQuery(id+"F21.imprint","IMPRINT",FACE,{"disambiguationData":[TD([[makeQuery(id+"F21.imprint","IMPRINT",EDGE,{"disambiguationData":[TD([[subQ2,1.0]])],"derivedFrom":subQ1}),-1.0]])]});}
            extrude(context, id + "F25", {"entities" : qUnion([Q0, Q1]), "operationType" : NewBodyOperationType.REMOVE, "oppositeDirection" : true, "depth" : 25.4 * mm});
        }
        {
            var Q0;
            Q0=makeQuery(id+"F19.opExtrude","SWEPT_FACE",FACE,{"disambiguationData":[OSD([sQuery(id+"F18.wireOp",EDGE,"E35.1")])]});
            var sketch = newSketch(context, id + "F26", { "sketchPlane" : qUnion([Q0])});
            skCircle(sketch, "E56", {"center": v(0, -38.1) * mm, "radius": 19.05 * mm});
            skSolve(sketch);
        }
        {
            var Q0;
            Q0=makeQuery(id+"F26.imprint","IMPRINT",FACE,{"disambiguationData":[TD([[makeQuery(id+"F26.imprint","IMPRINT",EDGE,{"derivedFrom":sQuery(id+"F26.wireOp",EDGE,"E56")}),1.0]])]});
            extrude(context, id + "F27", {"entities" : qUnion([Q0]), "depth" : 6.35 * mm});
        }
        {
            var Q0;
            Q0=makeQuery(id+"F27.opExtrude","CAP_FACE",FACE,{"disambiguationData":[OSD([sQuery(id+"F6.wireOp",EDGE,"E10.rect.top"),sQuery(id+"F18.wireOp",EDGE,"E35.1"),sQuery(id+"F26.wireOp",EDGE,"E56")])],"isStart":false});
            var sketch = newSketch(context, id + "F28", { "sketchPlane" : qUnion([Q0])});
            skLineSegment(sketch, "E57.rect.bottom", {"start": v(2, 2.4) * mm, "end": v(-2, 2.4) * mm});
            skLineSegment(sketch, "E57.rect.top", {"start": v(2, -21.57) * mm, "end": v(-2, -21.57) * mm});
            skLineSegment(sketch, "E57.rect.left", {"start": v(2, 2.4) * mm, "end": v(2, -21.57) * mm});
            skLineSegment(sketch, "E57.rect.right", {"start": v(-2, 2.4) * mm, "end": v(-2, -21.57) * mm});
            skCircle(sketch, "E58.0", {"center": v(0, 38.1) * mm, "radius": 38.1 * mm});
            skCircle(sketch, "E59.0", {"center": v(0, -38.1) * mm, "radius": 19.05 * mm});
            skPoint(sketch, "E60", {"position": v(0, -21.57) * mm});
            skSolve(sketch);
        }
        {
            var Q0;
            {var subQ5=sQuery(id+"F28.wireOp",EDGE,"E57.rect.top");Q0=makeQuery(id+"F28.imprint","IMPRINT",FACE,{"disambiguationData":[TD([[makeQuery(id+"F28.imprint","IMPRINT",EDGE,{"derivedFrom":subQ5}),-1.0]])]});}
            var Q1;
            {var subQ5=sQuery(id+"F28.wireOp",EDGE,"E57.rect.bottom");Q1=makeQuery(id+"F28.imprint","IMPRINT",FACE,{"disambiguationData":[TD([[makeQuery(id+"F28.imprint","IMPRINT",EDGE,{"derivedFrom":subQ5}),1.0]])]});}
            extrude(context, id + "F29", {"entities" : qUnion([Q0, Q1]), "operationType" : NewBodyOperationType.REMOVE, "oppositeDirection" : true, "depth" : 1.27 * mm});
        }
    });
